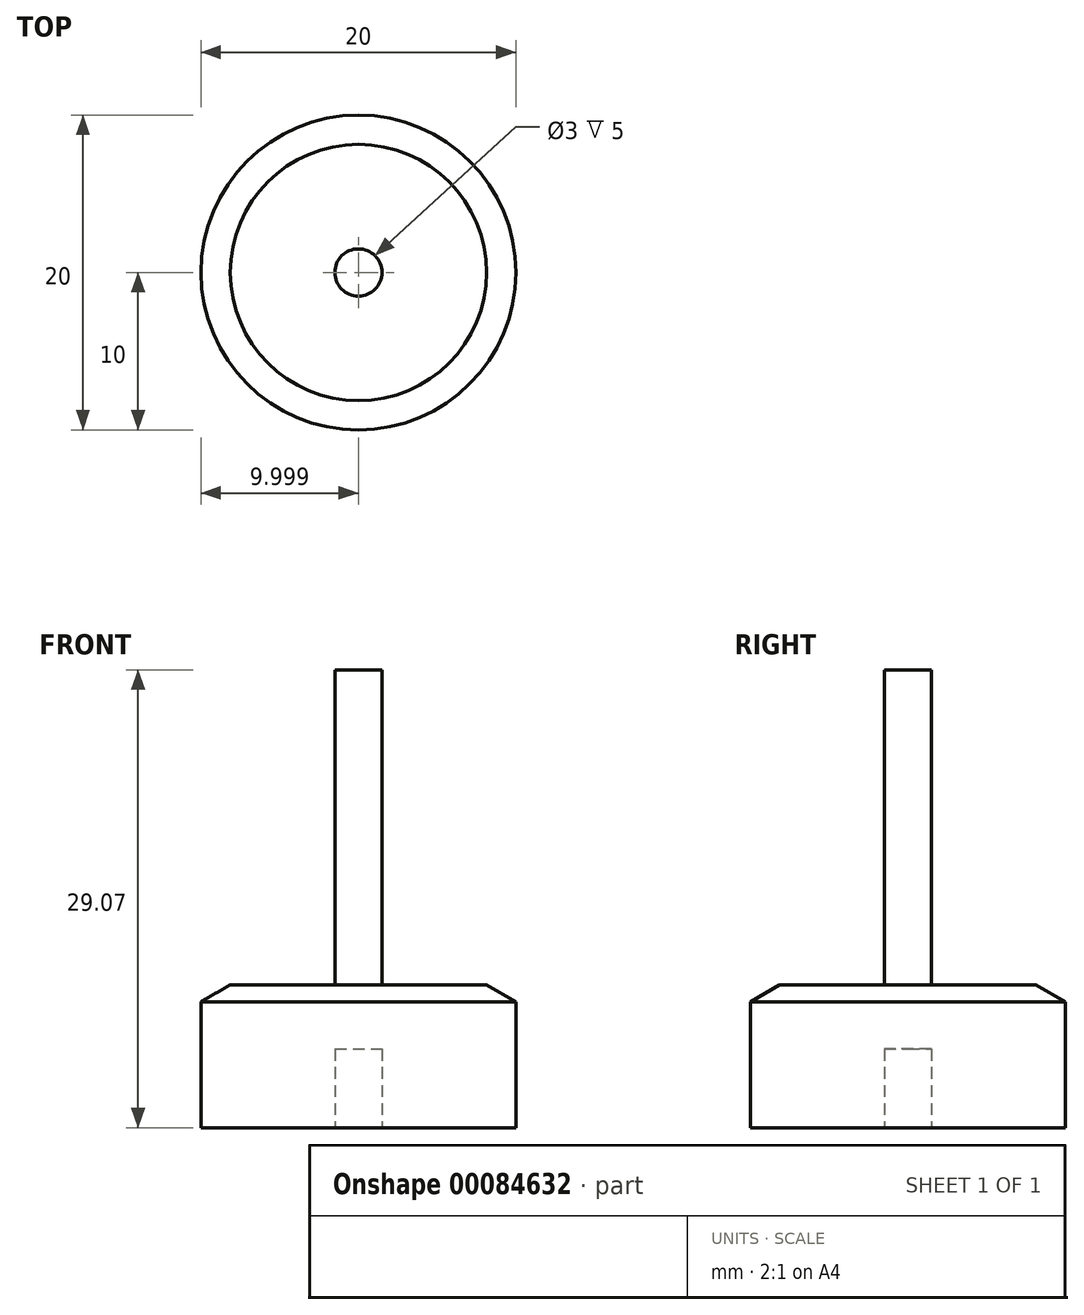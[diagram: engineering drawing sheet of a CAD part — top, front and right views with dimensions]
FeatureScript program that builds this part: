
annotation { "Feature Type Name" : "Feature", "Feature Type Description" : "" }
export const myFeature = defineFeature(function(context is Context, id is Id, definition is map)
    precondition{}
    {
        {
            var Q0;
            Q0=qCreatedBy(makeId("Front.planeOp"),FACE);
            var sketch = newSketch(context, id + "F0", { "sketchPlane" : qUnion([Q0])});
            skLineSegment(sketch, "E0.bottom", {"start": v(-30.55, 8) * mm, "end": v(-20.55, 8) * mm});
            skLineSegment(sketch, "E0.top", {"start": v(-30.55, 0) * mm, "end": v(-22.05, 0) * mm});
            skLineSegment(sketch, "E0.left", {"start": v(-30.55, 8) * mm, "end": v(-30.55, 0) * mm});
            skPoint(sketch, "E1", {"position": v(-20.55, 8) * mm});
            skPoint(sketch, "E2", {"position": v(-20.55, 0) * mm});
            skPoint(sketch, "E3", {"position": v(-20.55, 9.07) * mm});
            skLineSegment(sketch, "E4", {"start": v(-20.55, 8) * mm, "end": v(-20.55, 9.07) * mm});
            skLineSegment(sketch, "E5", {"start": v(-30.55, 8) * mm, "end": v(-28.7, 9.07) * mm});
            skLineSegment(sketch, "E6", {"start": v(-28.7, 9.07) * mm, "end": v(-20.55, 9.07) * mm});
            skLineSegment(sketch, "E7", {"start": v(-20.55, 8) * mm, "end": v(-20.55, 5) * mm});
            skPoint(sketch, "E0.right.end.orphan", {"position": v(-10.55, 0) * mm});
            skPoint(sketch, "E8.start.orphan", {"position": v(-10.55, 8) * mm});
            skLineSegment(sketch, "E9", {"start": v(-20.55, 9.07) * mm, "end": v(-20.55, 29.07) * mm});
            skLineSegment(sketch, "E10", {"start": v(-20.55, 29.07) * mm, "end": v(-22.05, 29.07) * mm});
            skLineSegment(sketch, "E11", {"start": v(-22.05, 29.07) * mm, "end": v(-22.05, 0) * mm});
            skPoint(sketch, "E12.start.orphan", {"position": v(-20.55, 4) * mm});
            skLineSegment(sketch, "E13", {"start": v(-20.55, 5) * mm, "end": v(-22.05, 5) * mm});
            skPoint(sketch, "E14", {"position": v(-20.55, 5) * mm});
            skSolve(sketch);
        }
        {
            var Q0;
            {var subQ0=sQuery(id+"F0.wireOp",EDGE,"E9");Q0=makeQuery(id+"F0.imprint","IMPRINT",FACE,{"disambiguationData":[TD([[makeQuery(id+"F0.imprint","IMPRINT",EDGE,{"derivedFrom":subQ0}),1.0]])]});}
            var Q1;
            {var subQ5=sQuery(id+"F0.wireOp",EDGE,"E0.top");Q1=makeQuery(id+"F0.imprint","IMPRINT",FACE,{"disambiguationData":[TD([[makeQuery(id+"F0.imprint","IMPRINT",EDGE,{"derivedFrom":subQ5}),1.0]])]});}
            var Q2;
            {var subQ0=sQuery(id+"F0.wireOp",EDGE,"E5");Q2=makeQuery(id+"F0.imprint","IMPRINT",FACE,{"disambiguationData":[TD([[makeQuery(id+"F0.imprint","IMPRINT",EDGE,{"derivedFrom":subQ0}),-1.0]])]});}
            var Q3;
            {var subQ0=sQuery(id+"F0.wireOp",EDGE,"E7");Q3=makeQuery(id+"F0.imprint","IMPRINT",FACE,{"disambiguationData":[TD([[makeQuery(id+"F0.imprint","IMPRINT",EDGE,{"derivedFrom":subQ0}),-1.0]])]});}
            var Q4;
            {var subQ0=sQuery(id+"F0.wireOp",EDGE,"E4");Q4=makeQuery(id+"F0.imprint","IMPRINT",FACE,{"disambiguationData":[TD([[makeQuery(id+"F0.imprint","IMPRINT",EDGE,{"derivedFrom":subQ0}),1.0]])]});}
            var Q5;
            Q5=sQuery(id+"F0.wireOp",EDGE,"E9");
            revolve(context, id + "F1", {"entities" : qUnion([Q0, Q1, Q2, Q3, Q4]), "axis" : qUnion([Q5]), "revolveType" : RevolveType.FULL});
        }
    });
